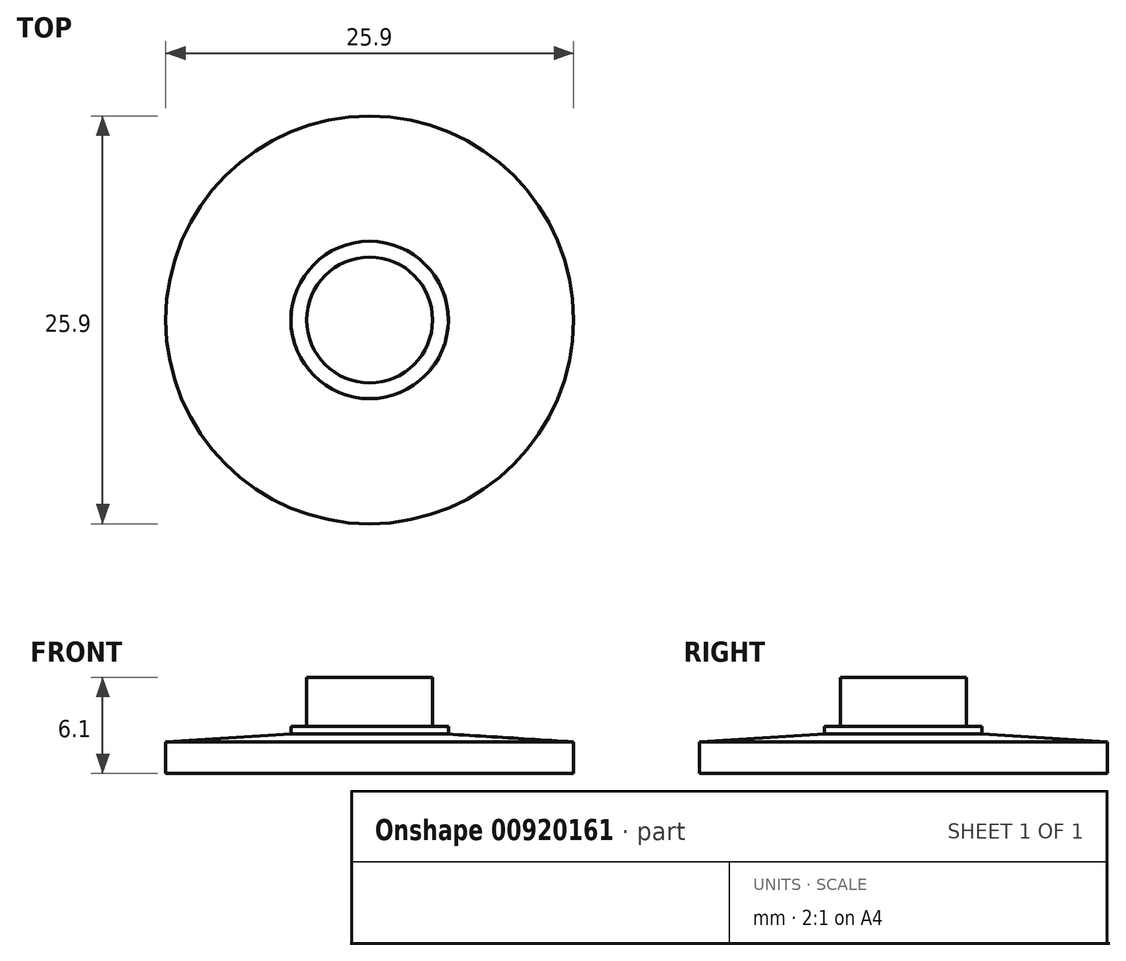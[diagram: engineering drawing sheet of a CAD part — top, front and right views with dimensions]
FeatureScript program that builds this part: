
annotation { "Feature Type Name" : "Feature", "Feature Type Description" : "" }
export const myFeature = defineFeature(function(context is Context, id is Id, definition is map)
    precondition{}
    {
        {
            var Q0;
            Q0=qCreatedBy(makeId("Top.planeOp"),FACE);
            var sketch = newSketch(context, id + "F0", { "sketchPlane" : qUnion([Q0])});
            skCircle(sketch, "E0", {"center": v(0, 0) * mm, "radius": 12.95 * mm});
            skCircle(sketch, "E1", {"center": v(0, 0) * mm, "radius": 4 * mm});
            skCircle(sketch, "E2", {"center": v(0, 0) * mm, "radius": 5 * mm});
            skSolve(sketch);
        }
        {
            var Q0;
            Q0=makeQuery(id+"F0.imprint","IMPRINT",FACE,{"disambiguationData":[TD([[makeQuery(id+"F0.imprint","IMPRINT",EDGE,{"derivedFrom":sQuery(id+"F0.wireOp",EDGE,"E1")}),1.0]])]});
            extrude(context, id + "F1", {"entities" : qUnion([Q0]), "depth" : 3.6 * mm, "offsetDistance" : 25 * mm});
        }
        {
            var Q0;
            Q0=makeQuery(id+"F0.imprint","IMPRINT",FACE,{"disambiguationData":[TD([[makeQuery(id+"F0.imprint","IMPRINT",EDGE,{"derivedFrom":sQuery(id+"F0.wireOp",EDGE,"E1")}),-1.0]])]});
            extrude(context, id + "F2", {"entities" : qUnion([Q0]), "operationType" : NewBodyOperationType.ADD, "depth" : .5 * mm, "offsetDistance" : 25 * mm});
        }
        {
            var Q0;
            Q0=makeQuery(id+"F0.imprint","IMPRINT",FACE,{"disambiguationData":[TD([[makeQuery(id+"F0.imprint","IMPRINT",EDGE,{"derivedFrom":sQuery(id+"F0.wireOp",EDGE,"E0")}),1.0]])]});
            var Q1;
            Q1=makeQuery(id+"F0.imprint","IMPRINT",FACE,{"disambiguationData":[TD([[makeQuery(id+"F0.imprint","IMPRINT",EDGE,{"derivedFrom":sQuery(id+"F0.wireOp",EDGE,"E1")}),-1.0]])]});
            var Q2;
            Q2=makeQuery(id+"F0.imprint","IMPRINT",FACE,{"disambiguationData":[TD([[makeQuery(id+"F0.imprint","IMPRINT",EDGE,{"derivedFrom":sQuery(id+"F0.wireOp",EDGE,"E1")}),1.0]])]});
            extrude(context, id + "F3", {"entities" : qUnion([Q0, Q1, Q2]), "oppositeDirection" : true, "depth" : 2.5 * mm, "offsetDistance" : 25 * mm});
        }
        {
            var Q0;
            Q0=makeQuery(id+"F3.opExtrude","CAP_FACE",FACE,{"disambiguationData":[OSD([sQuery(id+"F0.wireOp",EDGE,"E0")])],"isStart":true});
            chamfer(context, id + "F4", {"entities" : qUnion([Q0]), "chamferType" : ChamferType.TWO_OFFSETS, "width1" : .5 * mm, "oppositeDirection" : true, "width2" : 8 * mm, "tangentPropagation" : true});
        }
    });
